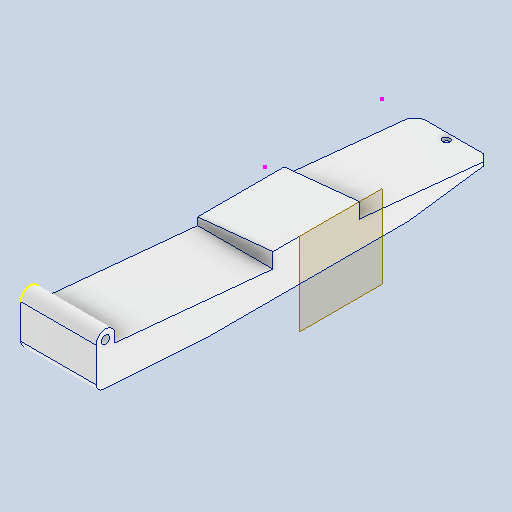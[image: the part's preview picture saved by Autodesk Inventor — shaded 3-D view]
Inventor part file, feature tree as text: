
AUTODESK INVENTOR PART (.ipt)
format: ipt  version: 2025 (Build 290162010, 162A)  size: 224,768 bytes
history: native  units: mm
features: chamfer x6, sketch x5, hole x3, extrude x2, fillet x2, plane x1, other x1
ambient origin geometry x8: Origin, YZ Plane, XZ Plane, XY Plane, X Axis, Y Axis, Z Axis, Center Point
bodies: Volumenkörper1 (feature_tree)
feature tree (20):
  extrude  "Extrusion1"  Depth=20.0mm
  extrude  "Extrusion3"  Depth=5.0mm
  fillet  "Rundung2"  Radius=8.5mm
  hole  "Bohrung1"  [1 undecoded]
  chamfer  "Fasen2"  Distance=42.0mm Angle=45.0deg
  chamfer  "Fasen3"  Distance=35.0mm Angle=45.0deg
  plane  "Arbeitsebene1"
  hole  "Bohrung3"  [1 undecoded]
  chamfer  "Fasen5"  Distance=3.0mm Angle=45.0deg
  hole  "Bohrung4"  [1 undecoded]
  chamfer  "Fasen6"  Distance=20.0mm Angle=45.0deg
  other  "Verdickung1"
  chamfer  "Fasen7"  Distance=2.0mm Angle=45.0deg
  chamfer  "Fasen8"  Distance=2.0mm
  fillet  "Rundung4"  [1 undecoded]
  sketch  "Skizze1"  dims[d0=7.0mm d1=0.0mm d2=20.0mm]
  sketch  "Skizze3"  dims[d3=105.0mm d8=5.0mm d9=8.5mm d10=0.0mm]
  sketch  "Skizze4"  dims[d11=2.5mm]
  sketch  "Skizze7"  dims[d13=2.2mm d14=6.0mm d15=4.0mm d16=2.0mm d17=90.0deg d18=5.0mm d19=20.594885mm d34=2.0mm d35=2.0mm d36=45.0deg d37=4.0mm d38=42.0mm d39=45.0deg]
  sketch  "Skizze8"  dims[d40=2.2mm d41=6.0mm d42=4.0mm d43=2.0mm d44=90.0deg d45=5.0mm d46=20.594885mm d50=35.0mm d51=3.5mm d52=45.0deg d53=2.0mm d54=2.0mm d55=5.0mm d56=4.0mm d57=2.0mm d58=90.0deg d59=6.3mm d60=20.594885mm d61=3.0mm d62=22.0mm d63=45.0deg d64=4.0mm d65=1.0mm d66=20.0mm d67=2.0mm d68=45.0deg d69=30.0mm d70=2.0mm d71=45.0deg d72=2.0mm]
note: 4 required parameter values undecoded (feature->parameter linkage not recoverable at this tier; creation-order binding heuristic only, values carry confidence <= 0.55)
